# Revit family: Mobile-Work-Tools-Teknion-HDAB_Add_On_Boards-R2021
name_source: partatom
category: Furniture
units: mm (PartAtom-declared; Revit-internal decimal feet)

## family parameters
Always vertical = Yes
Cut with Voids When Loaded = No
OmniClass Number = 23.40.20.00
OmniClass Title = General Furniture and Specialties
Room Calculation Point = No
Shared = Yes
Work Plane-Based = No

## types (3) — shared parameters
Assembly Code = E2020200
Manufacturer = Teknion
Manufacturer Fax = 416.661.4586
Part Number = HDAB
Product Documentation Link = https://assets.teknion.com
Product Line = Kiosk
Product Page URL = https://www.teknion.com
Series = Kiosk
Sustainability Data = https://www.teknion.com
URL = www.teknion.com
Unit Weight URL = http://www.teknion.com
Warranty = http://www.teknion.com
Whiteboard Finish = Laminate-Teknion-5D-Whiteboard
zero-valued in all types: Default Elevation

## per-type parameters (varying)
| type | Description | Model | Tackboard Finish |
| One Whiteboard Add Ons & One Tackboard Add Ons | Add-On Boards, One Whiteboard Add-Ons & One Tackboard Add-Ons | HDABU | Fabric - Teknion - Heather Tech - R256 - Thistle Tech |
| Two Tackboard Add Ons | Add-On Boards, Two Tackboard Add-Ons | HDABT | Fabric-Teknion-T754-Actuate-Thermal |
| Two Whiteboard Add Ons | Add-On Boards, Two Whiteboard Add-Ons | HDABW | Fabric - Teknion - D409 - India - Surat |

type visibility flags: 3 boolean params named "<type name>" — each type sets only its own to Yes (folded from table)

## geometry (parser evidence)
native form markers: Sweep x2
no freeform markers — native parametric forms only
